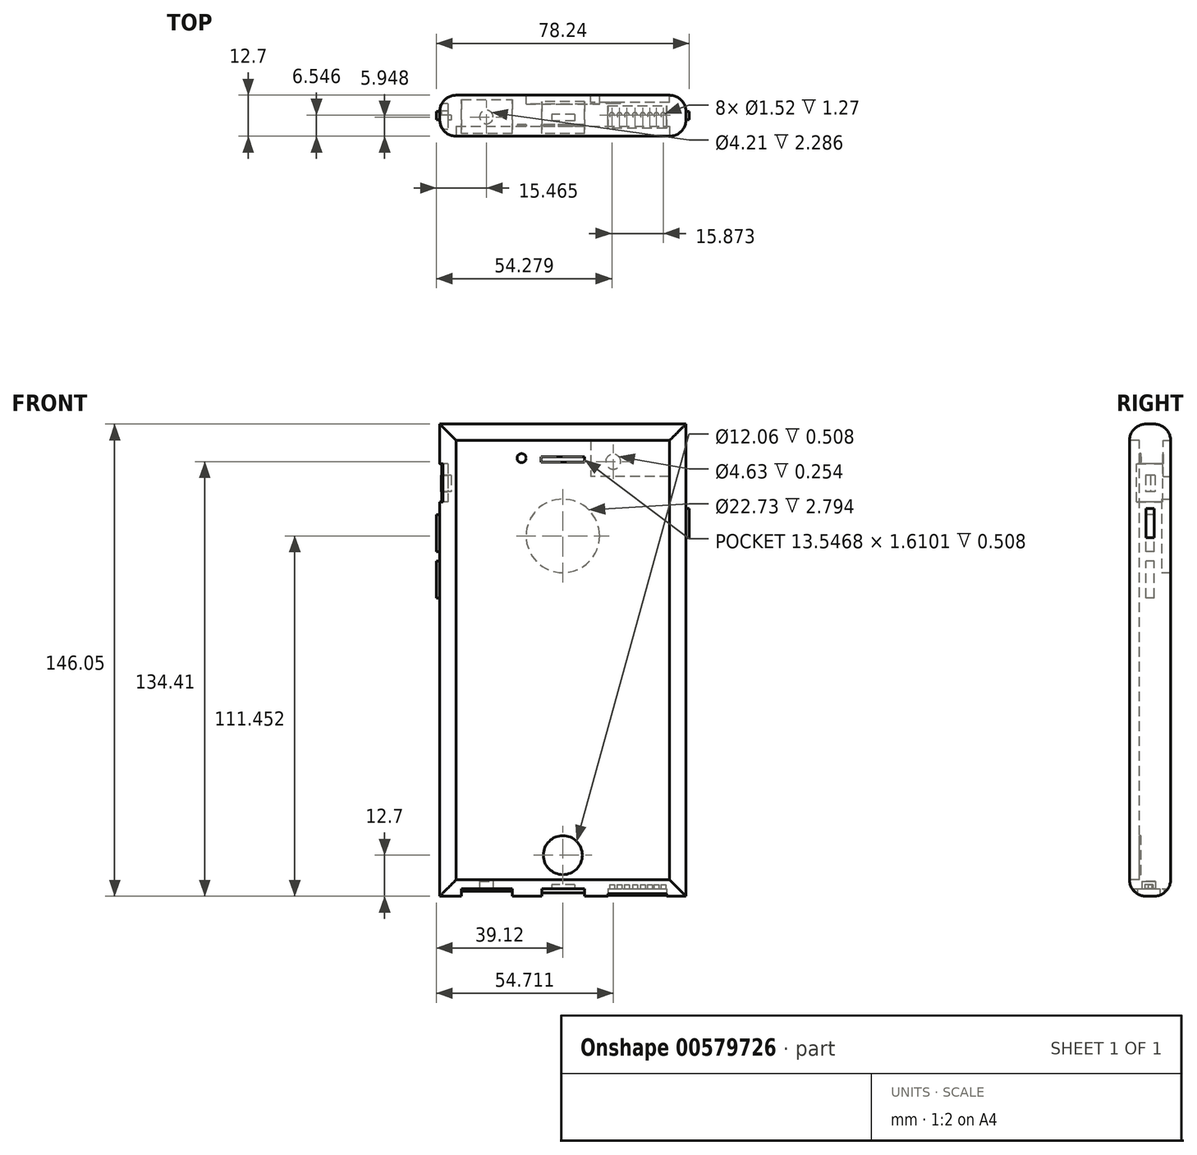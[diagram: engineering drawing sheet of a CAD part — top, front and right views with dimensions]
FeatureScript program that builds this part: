
annotation { "Feature Type Name" : "Feature", "Feature Type Description" : "" }
export const myFeature = defineFeature(function(context is Context, id is Id, definition is map)
    precondition{}
    {
        {
            var Q0;
            Q0=qCreatedBy(makeId("Front.planeOp"),FACE);
            var sketch = newSketch(context, id + "F0", { "sketchPlane" : qUnion([Q0])});
            skLineSegment(sketch, "E0.bottom", {"start": v(0, 0) * mm, "end": v(76.2, 0) * mm});
            skLineSegment(sketch, "E0.top", {"start": v(0, 146.05) * mm, "end": v(76.2, 146.05) * mm});
            skLineSegment(sketch, "E0.left", {"start": v(0, 0) * mm, "end": v(0, 146.05) * mm});
            skLineSegment(sketch, "E0.right", {"start": v(76.2, 0) * mm, "end": v(76.2, 146.05) * mm});
            skSolve(sketch);
        }
        {
            var Q0;
            Q0=makeQuery(id+"F0.imprint","IMPRINT",FACE,{"disambiguationData":[TD([[makeQuery(id+"F0.imprint","IMPRINT",EDGE,{"derivedFrom":sQuery(id+"F0.wireOp",EDGE,"E0.bottom")}),1.0]])]});
            extrude(context, id + "F1", {"entities" : qUnion([Q0]), "depth" : 12.7 * mm, "offsetDistance" : 25.4 * mm});
        }
        {
            var Q0;
            Q0=makeQuery(id+"F1.opExtrude","CAP_FACE",FACE,{"disambiguationData":[OSD([sQuery(id+"F0.wireOp",EDGE,"E0.bottom"),sQuery(id+"F0.wireOp",EDGE,"E0.top"),sQuery(id+"F0.wireOp",EDGE,"E0.left"),sQuery(id+"F0.wireOp",EDGE,"E0.right")])],"isStart":false});
            fillet(context, id + "F2", {"entities" : qUnion([Q0]), "radius" : 5.08 * mm, "tangentPropagation" : true, "allowEdgeOverflow" : false});
        }
        {
            var Q0;
            Q0=makeQuery(id+"F1.opExtrude","CAP_FACE",FACE,{"disambiguationData":[OSD([sQuery(id+"F0.wireOp",EDGE,"E0.bottom"),sQuery(id+"F0.wireOp",EDGE,"E0.top"),sQuery(id+"F0.wireOp",EDGE,"E0.left"),sQuery(id+"F0.wireOp",EDGE,"E0.right")])],"isStart":true});
            fillet(context, id + "F3", {"entities" : qUnion([Q0]), "radius" : 5.08 * mm, "tangentPropagation" : true, "allowEdgeOverflow" : false});
        }
        {
            var Q0;
            Q0=makeQuery(id+"F1.opExtrude","CAP_FACE",FACE,{"disambiguationData":[OSD([sQuery(id+"F0.wireOp",EDGE,"E0.bottom"),sQuery(id+"F0.wireOp",EDGE,"E0.top"),sQuery(id+"F0.wireOp",EDGE,"E0.left"),sQuery(id+"F0.wireOp",EDGE,"E0.right")])],"isStart":false});
            extrude(context, id + "F4", {"entities" : qUnion([Q0]), "operationType" : NewBodyOperationType.REMOVE, "oppositeDirection" : true, "depth" : 2.54 * mm, "offsetDistance" : 25.4 * mm});
        }
        {
            var Q0;
            Q0=makeQuery(id+"F1.opExtrude","SWEPT_FACE",FACE,{"disambiguationData":[OSD([sQuery(id+"F0.wireOp",EDGE,"E0.left")])]});
            var sketch = newSketch(context, id + "F5", { "sketchPlane" : qUnion([Q0])});
            skLineSegment(sketch, "E1.bottom", {"start": v(2.58, 133.75) * mm, "end": v(10.56, 133.75) * mm});
            skLineSegment(sketch, "E1.top", {"start": v(2.58, 122) * mm, "end": v(10.56, 122) * mm});
            skLineSegment(sketch, "E1.left", {"start": v(2.58, 133.75) * mm, "end": v(2.58, 122) * mm});
            skLineSegment(sketch, "E1.right", {"start": v(10.56, 133.75) * mm, "end": v(10.56, 122) * mm});
            skSolve(sketch);
        }
        {
            var Q0;
            {var subQ0=sQuery(id+"F5.wireOp",EDGE,"E1.left");Q0=makeQuery(id+"F5.imprint","IMPRINT",FACE,{"disambiguationData":[TD([[makeQuery(id+"F5.imprint","IMPRINT",EDGE,{"derivedFrom":subQ0}),1.0]])]});}
            var Q1;
            {var subQ0=sQuery(id+"F5.wireOp",EDGE,"E1.bottom");var subQ1=sQuery(id+"F0.wireOp",EDGE,"E0.left");var subQ2=makeQuery(id+"F1.opExtrude","SWEPT_FACE",FACE,{"disambiguationData":[OSD([subQ1])]});var subQ3=makeQuery(id+"F3.opFillet","BLEND_EDGE",EDGE,{"blendedFrom":[makeQuery(id+"F1.opExtrude","CAP_EDGE",EDGE,{"disambiguationData":[OSD([subQ1])],"isStart":true}),subQ2],"blendedInto":[subQ2]});var subQ4=makeQuery(id+"F5.imprint","INTERSECT",VERTEX,{"derivedFrom":[subQ3,subQ0]});Q1=makeQuery(id+"F5.imprint","IMPRINT",FACE,{"disambiguationData":[TD([[makeQuery(id+"F5.imprint","IMPRINT",EDGE,{"disambiguationData":[TD([[subQ4,-1.0]])],"derivedFrom":subQ0}),-1.0]])]});}
            var Q2;
            {var subQ0=sQuery(id+"F5.wireOp",EDGE,"E1.right");Q2=makeQuery(id+"F5.imprint","IMPRINT",FACE,{"disambiguationData":[TD([[makeQuery(id+"F5.imprint","IMPRINT",EDGE,{"derivedFrom":subQ0}),-1.0]])]});}
            extrude(context, id + "F6", {"entities" : qUnion([Q0, Q1, Q2]), "operationType" : NewBodyOperationType.REMOVE, "oppositeDirection" : true, "depth" : 2.54 * mm, "offsetDistance" : 25.4 * mm});
        }
        {
            var Q0;
            Q0=makeQuery(id+"F6.boolean.opBoolean","COPY",FACE,{"derivedFrom":makeQuery(id+"F6.opExtrude","CAP_FACE",FACE,{"disambiguationData":[OSD([sQuery(id+"F5.wireOp",EDGE,"E1.bottom"),sQuery(id+"F5.wireOp",EDGE,"E1.top"),sQuery(id+"F5.wireOp",EDGE,"E1.left"),sQuery(id+"F5.wireOp",EDGE,"E1.right")])],"isStart":false})});
            var sketch = newSketch(context, id + "F7", { "sketchPlane" : qUnion([Q0])});
            skLineSegment(sketch, "E2.bottom", {"start": v(4.8, 130.2) * mm, "end": v(7.68, 130.2) * mm});
            skLineSegment(sketch, "E2.top", {"start": v(4.8, 125.1) * mm, "end": v(7.68, 125.1) * mm});
            skLineSegment(sketch, "E2.left", {"start": v(4.8, 130.2) * mm, "end": v(4.8, 125.1) * mm});
            skLineSegment(sketch, "E2.right", {"start": v(7.68, 130.2) * mm, "end": v(7.68, 125.1) * mm});
            skSolve(sketch);
        }
        {
            var Q0;
            Q0 = qSketchRegion(id + "F7", true);
            extrude(context, id + "F8", {"entities" : qUnion([Q0]), "operationType" : NewBodyOperationType.ADD, "depth" : 2.03 * mm, "offsetDistance" : 25.4 * mm});
        }
        {
            var Q0;
            Q0=makeQuery(id+"F8.opExtrude","CAP_FACE",FACE,{"disambiguationData":[OSD([sQuery(id+"F7.wireOp",EDGE,"E2.bottom"),sQuery(id+"F7.wireOp",EDGE,"E2.top"),sQuery(id+"F7.wireOp",EDGE,"E2.left"),sQuery(id+"F7.wireOp",EDGE,"E2.right")])],"isStart":false});
            var sketch = newSketch(context, id + "F9", { "sketchPlane" : qUnion([Q0])});
            skLineSegment(sketch, "E3", {"start": v(7.68, 125.1) * mm, "end": v(7.68, 130.2) * mm});
            skLineSegment(sketch, "E4", {"start": v(7.68, 130.2) * mm, "end": v(6.24, 130.2) * mm});
            skLineSegment(sketch, "E5", {"start": v(6.24, 130.2) * mm, "end": v(6.24, 125.1) * mm});
            skLineSegment(sketch, "E6", {"start": v(6.24, 125.1) * mm, "end": v(7.68, 125.1) * mm});
            skSolve(sketch);
        }
        {
            var Q0;
            Q0=makeQuery(id+"F9.imprint","IMPRINT",FACE,{"disambiguationData":[TD([[makeQuery(id+"F9.imprint","IMPRINT",EDGE,{"derivedFrom":sQuery(id+"F9.wireOp",EDGE,"E3")}),-1.0]])]});
            extrude(context, id + "F10", {"entities" : qUnion([Q0]), "operationType" : NewBodyOperationType.REMOVE, "oppositeDirection" : true, "depth" : 3.05 * mm, "offsetDistance" : 25.4 * mm});
        }
        {
            var Q0;
            {var subQ0=sQuery(id+"F0.wireOp",EDGE,"E0.bottom");var subQ1=sQuery(id+"F0.wireOp",EDGE,"E0.left");Q0=makeQuery(id+"F6.boolean.opBoolean","SPLIT",FACE,{"disambiguationData":[TD([makeQuery(id+"F1.opExtrude","SWEPT_FACE",FACE,{"disambiguationData":[OSD([subQ0])]})])],"derivedFrom":makeQuery(id+"F1.opExtrude","SWEPT_FACE",FACE,{"disambiguationData":[OSD([subQ1])]})});}
            var sketch = newSketch(context, id + "F11", { "sketchPlane" : qUnion([Q0])});
            skLineSegment(sketch, "E7.bottom", {"start": v(5.08, 118.03) * mm, "end": v(7.62, 118.03) * mm});
            skLineSegment(sketch, "E7.top", {"start": v(5.08, 106.6) * mm, "end": v(7.62, 106.6) * mm});
            skLineSegment(sketch, "E7.left", {"start": v(5.08, 118.03) * mm, "end": v(5.08, 106.6) * mm});
            skLineSegment(sketch, "E7.right", {"start": v(7.62, 118.03) * mm, "end": v(7.62, 106.6) * mm});
            skSolve(sketch);
        }
        {
            var Q0;
            Q0=makeQuery(id+"F11.imprint","IMPRINT",FACE,{"disambiguationData":[TD([[makeQuery(id+"F11.imprint","IMPRINT",EDGE,{"derivedFrom":sQuery(id+"F11.wireOp",EDGE,"E7.bottom")}),-1.0]])]});
            extrude(context, id + "F12", {"entities" : qUnion([Q0]), "operationType" : NewBodyOperationType.ADD, "depth" : 1.02 * mm, "offsetDistance" : 25.4 * mm});
        }
        {
            var Q0;
            {var subQ0=sQuery(id+"F0.wireOp",EDGE,"E0.bottom");var subQ2=sQuery(id+"F0.wireOp",EDGE,"E0.left");var subQ5=makeQuery(id+"F1.opExtrude","SWEPT_FACE",FACE,{"disambiguationData":[OSD([subQ0])]});Q0=makeQuery(id+"F12.boolean.opBoolean","SPLIT",FACE,{"disambiguationData":[TD([subQ5])],"derivedFrom":makeQuery(id+"F6.boolean.opBoolean","SPLIT",FACE,{"disambiguationData":[TD([subQ5])],"derivedFrom":makeQuery(id+"F1.opExtrude","SWEPT_FACE",FACE,{"disambiguationData":[OSD([subQ2])]})})});}
            var sketch = newSketch(context, id + "F13", { "sketchPlane" : qUnion([Q0])});
            skLineSegment(sketch, "E8.bottom", {"start": v(5.08, 103.7) * mm, "end": v(7.62, 103.7) * mm});
            skLineSegment(sketch, "E8.top", {"start": v(5.08, 92.27) * mm, "end": v(7.62, 92.27) * mm});
            skLineSegment(sketch, "E8.left", {"start": v(5.08, 103.7) * mm, "end": v(5.08, 92.27) * mm});
            skLineSegment(sketch, "E8.right", {"start": v(7.62, 103.7) * mm, "end": v(7.62, 92.27) * mm});
            skSolve(sketch);
        }
        {
            var Q0;
            Q0=makeQuery(id+"F13.imprint","IMPRINT",FACE,{"disambiguationData":[TD([[makeQuery(id+"F13.imprint","IMPRINT",EDGE,{"derivedFrom":sQuery(id+"F13.wireOp",EDGE,"E8.bottom")}),-1.0]])]});
            extrude(context, id + "F14", {"entities" : qUnion([Q0]), "operationType" : NewBodyOperationType.ADD, "depth" : 1.02 * mm, "offsetDistance" : 25.4 * mm});
        }
        {
            var Q0;
            Q0=makeQuery(id+"F4.boolean.opBoolean","COPY",FACE,{"derivedFrom":makeQuery(id+"F4.opExtrude","CAP_FACE",FACE,{"disambiguationData":[OSD([sQuery(id+"F0.wireOp",EDGE,"E0.bottom"),sQuery(id+"F0.wireOp",EDGE,"E0.top"),sQuery(id+"F0.wireOp",EDGE,"E0.left"),sQuery(id+"F0.wireOp",EDGE,"E0.right")])],"isStart":false})});
            var sketch = newSketch(context, id + "F15", { "sketchPlane" : qUnion([Q0])});
            skLineSegment(sketch, "E9", {"start": v(5.08, 5.08) * mm, "end": v(38.1, 5.08) * mm});
            skLineSegment(sketch, "E10", {"start": v(38.1, 5.08) * mm, "end": v(38.1, 12.7) * mm});
            skCircle(sketch, "E11", {"center": v(38.1, 12.7) * mm, "radius": 6.03 * mm});
            skSolve(sketch);
        }
        {
            var Q0;
            Q0=makeQuery(id+"F15.imprint","IMPRINT",FACE,{"disambiguationData":[TD([[makeQuery(id+"F15.imprint","IMPRINT",EDGE,{"derivedFrom":sQuery(id+"F15.wireOp",EDGE,"E11")}),1.0]])]});
            extrude(context, id + "F16", {"entities" : qUnion([Q0]), "operationType" : NewBodyOperationType.REMOVE, "oppositeDirection" : true, "depth" : 0.5 * mm, "offsetDistance" : 25.4 * mm});
        }
        {
            var Q0;
            Q0=makeQuery(id+"F1.opExtrude","SWEPT_FACE",FACE,{"disambiguationData":[OSD([sQuery(id+"F0.wireOp",EDGE,"E0.bottom")])]});
            var sketch = newSketch(context, id + "F17", { "sketchPlane" : qUnion([Q0])});
            skLineSegment(sketch, "E12.bottom", {"start": v(6.77, 11.85) * mm, "end": v(22.5, 11.85) * mm});
            skLineSegment(sketch, "E12.top", {"start": v(6.77, 1.38) * mm, "end": v(22.5, 1.38) * mm});
            skLineSegment(sketch, "E12.left", {"start": v(6.77, 11.85) * mm, "end": v(6.77, 1.38) * mm});
            skLineSegment(sketch, "E12.right", {"start": v(22.5, 11.85) * mm, "end": v(22.5, 1.38) * mm});
            skSolve(sketch);
        }
        {
            var Q0;
            Q0 = qSketchRegion(id + "F17", true);
            var Q1;
            {var subQ0=sQuery(id+"F17.wireOp",EDGE,"E12.bottom");Q1=makeQuery(id+"F17.imprint","IMPRINT",FACE,{"disambiguationData":[TD([[makeQuery(id+"F17.imprint","IMPRINT",EDGE,{"derivedFrom":subQ0}),-1.0]])]});}
            extrude(context, id + "F18", {"entities" : qUnion([Q0, Q1]), "operationType" : NewBodyOperationType.REMOVE, "oppositeDirection" : true, "depth" : 2.3 * mm, "offsetDistance" : 25.4 * mm});
        }
        {
            var Q0;
            {var subQ0=sQuery(id+"F0.wireOp",EDGE,"E0.bottom");var subQ2=sQuery(id+"F0.wireOp",EDGE,"E0.right");var subQ5=makeQuery(id+"F1.opExtrude","SWEPT_FACE",FACE,{"disambiguationData":[OSD([subQ2])]});Q0=makeQuery(id+"FUvdi6jXHZb6WJ3_1.boolean.opBoolean","SPLIT",FACE,{"disambiguationData":[TD([subQ5])],"derivedFrom":makeQuery(id+"F18.boolean.opBoolean","SPLIT",FACE,{"disambiguationData":[TD([subQ5])],"derivedFrom":makeQuery(id+"F1.opExtrude","SWEPT_FACE",FACE,{"disambiguationData":[OSD([subQ0])]})})});}
            var sketch = newSketch(context, id + "F19", { "sketchPlane" : qUnion([Q0])});
            skLineSegment(sketch, "E13.bottom", {"start": v(52.05, 10.24) * mm, "end": v(70.18, 10.24) * mm});
            skLineSegment(sketch, "E13.top", {"start": v(52.05, 3.29) * mm, "end": v(70.18, 3.29) * mm});
            skLineSegment(sketch, "E13.left", {"start": v(52.05, 10.24) * mm, "end": v(52.05, 3.29) * mm});
            skLineSegment(sketch, "E13.right", {"start": v(70.18, 10.24) * mm, "end": v(70.18, 3.29) * mm});
            skSolve(sketch);
        }
        {
            var Q0;
            {var subQ0=sQuery(id+"F19.wireOp",EDGE,"E13.top");Q0=makeQuery(id+"F19.imprint","IMPRINT",FACE,{"disambiguationData":[TD([[makeQuery(id+"F19.imprint","IMPRINT",EDGE,{"derivedFrom":subQ0}),1.0]])]});}
            var Q1;
            {var subQ0=sQuery(id+"F19.wireOp",EDGE,"E13.left");var subQ1=sQuery(id+"F0.wireOp",EDGE,"E0.right");var subQ3=sQuery(id+"F0.wireOp",EDGE,"E0.bottom");var subQ5=makeQuery(id+"F1.opExtrude","SWEPT_FACE",FACE,{"disambiguationData":[OSD([subQ1])]});var subQ6=makeQuery(id+"F1.opExtrude","SWEPT_FACE",FACE,{"disambiguationData":[OSD([subQ3])]});var subQ9=makeQuery(id+"FUvdi6jXHZb6WJ3_1.boolean.opBoolean","SPLIT",EDGE,{"disambiguationData":[TD([subQ5])],"derivedFrom":makeQuery(id+"F18.boolean.opBoolean","SPLIT",EDGE,{"disambiguationData":[TD([subQ5])],"derivedFrom":makeQuery(id+"F2.opFillet","BLEND_EDGE",EDGE,{"blendedFrom":[makeQuery(id+"F1.opExtrude","CAP_EDGE",EDGE,{"disambiguationData":[OSD([subQ3])],"isStart":false}),subQ6],"blendedInto":[subQ6]})})});var subQ10=makeQuery(id+"F19.imprint","INTERSECT",VERTEX,{"derivedFrom":[subQ9,subQ0]});Q1=makeQuery(id+"F19.imprint","IMPRINT",FACE,{"disambiguationData":[TD([[makeQuery(id+"F19.imprint","IMPRINT",EDGE,{"disambiguationData":[TD([[subQ10,-1.0]])],"derivedFrom":subQ0}),1.0]])]});}
            var Q2;
            {var subQ0=sQuery(id+"F19.wireOp",EDGE,"E13.bottom");Q2=makeQuery(id+"F19.imprint","IMPRINT",FACE,{"disambiguationData":[TD([[makeQuery(id+"F19.imprint","IMPRINT",EDGE,{"derivedFrom":subQ0}),-1.0]])]});}
            extrude(context, id + "F20", {"entities" : qUnion([Q0, Q1, Q2]), "operationType" : NewBodyOperationType.REMOVE, "oppositeDirection" : true, "depth" : 2.3 * mm, "offsetDistance" : 25.4 * mm});
        }
        {
            var Q0;
            Q0=makeQuery(id+"F18.boolean.opBoolean","COPY",FACE,{"derivedFrom":makeQuery(id+"F18.opExtrude","CAP_FACE",FACE,{"disambiguationData":[OSD([sQuery(id+"F17.wireOp",EDGE,"E12.bottom"),sQuery(id+"F17.wireOp",EDGE,"E12.top"),sQuery(id+"F17.wireOp",EDGE,"E12.left"),sQuery(id+"F17.wireOp",EDGE,"E12.right")])],"isStart":false})});
            var sketch = newSketch(context, id + "F21", { "sketchPlane" : qUnion([Q0])});
            skCircle(sketch, "E14", {"center": v(14.44, 6.75) * mm, "radius": 2.1 * mm});
            skSolve(sketch);
        }
        {
            var Q0;
            Q0 = qSketchRegion(id + "F21", true);
            extrude(context, id + "F22", {"entities" : qUnion([Q0]), "operationType" : NewBodyOperationType.REMOVE, "oppositeDirection" : true, "depth" : 2.3 * mm, "offsetDistance" : 25.4 * mm});
        }
        {
            var Q0;
            Q0=makeQuery(id+"F20.boolean.opBoolean","COPY",FACE,{"derivedFrom":makeQuery(id+"F20.opExtrude","CAP_FACE",FACE,{"disambiguationData":[OSD([sQuery(id+"F19.wireOp",EDGE,"E13.bottom"),sQuery(id+"F19.wireOp",EDGE,"E13.top"),sQuery(id+"F19.wireOp",EDGE,"E13.left"),sQuery(id+"F19.wireOp",EDGE,"E13.right")])],"isStart":false})});
            var sketch = newSketch(context, id + "F23", { "sketchPlane" : qUnion([Q0])});
            skLineSegment(sketch, "E15", {"start": v(52.05, 6.15) * mm, "end": v(70.18, 6.15) * mm});
            skCircle(sketch, "E16", {"center": v(53.26, 6.15) * mm, "radius": 0.76 * mm});
            skCircle(sketch, "E17", {"center": v(55.62, 6.15) * mm, "radius": 0.76 * mm});
            skCircle(sketch, "E18", {"center": v(57.9, 6.15) * mm, "radius": 0.76 * mm});
            skCircle(sketch, "E19", {"center": v(60.4, 6.15) * mm, "radius": 0.76 * mm});
            skCircle(sketch, "E20", {"center": v(62.83, 6.15) * mm, "radius": 0.76 * mm});
            skCircle(sketch, "E21", {"center": v(65.04, 6.15) * mm, "radius": 0.76 * mm});
            skCircle(sketch, "E22", {"center": v(67.06, 6.15) * mm, "radius": 0.76 * mm});
            skCircle(sketch, "E23", {"center": v(69.13, 6.15) * mm, "radius": 0.76 * mm});
            skSolve(sketch);
        }
        {
            var Q0;
            Q0 = qSketchRegion(id + "F23", true);
            extrude(context, id + "F24", {"entities" : qUnion([Q0]), "operationType" : NewBodyOperationType.REMOVE, "oppositeDirection" : true, "depth" : 1.27 * mm, "offsetDistance" : 25.4 * mm});
        }
        {
            var Q0;
            Q0=makeQuery(id+"F16.boolean.opBoolean","COPY",FACE,{"derivedFrom":makeQuery(id+"F16.opExtrude","CAP_FACE",FACE,{"disambiguationData":[OSD([sQuery(id+"F15.wireOp",EDGE,"E11")])],"isStart":false})});
            var sketch = newSketch(context, id + "F25", { "sketchPlane" : qUnion([Q0])});
            skLineSegment(sketch, "E24.bottom", {"start": v(44.87, 135.88) * mm, "end": v(31.33, 135.88) * mm});
            skLineSegment(sketch, "E24.top", {"start": v(44.87, 134.27) * mm, "end": v(31.33, 134.27) * mm});
            skLineSegment(sketch, "E24.left", {"start": v(44.87, 135.88) * mm, "end": v(44.87, 134.27) * mm});
            skLineSegment(sketch, "E24.right", {"start": v(31.33, 135.88) * mm, "end": v(31.33, 134.27) * mm});
            skPoint(sketch, "E24.middle", {"position": v(38.1, 135.08) * mm});
            skSolve(sketch);
        }
        {
            var Q0;
            Q0 = qSketchRegion(id + "F25", true);
            var Q1;
            Q1=makeQuery(id+"F4.boolean.opBoolean","COPY",FACE,{"derivedFrom":makeQuery(id+"F4.opExtrude","CAP_FACE",FACE,{"disambiguationData":[OSD([sQuery(id+"F0.wireOp",EDGE,"E0.bottom"),sQuery(id+"F0.wireOp",EDGE,"E0.top"),sQuery(id+"F0.wireOp",EDGE,"E0.left"),sQuery(id+"F0.wireOp",EDGE,"E0.right")])],"isStart":false})});
            extrude(context, id + "F26", {"entities" : qUnion([Q0, Q1]), "operationType" : NewBodyOperationType.REMOVE, "oppositeDirection" : true, "depth" : 0.5 * mm, "offsetDistance" : 25.4 * mm});
        }
        {
            var Q0;
            Q0=makeQuery(id+"F26.boolean.opBoolean","MERGE",FACE,{"derivedFrom":[makeQuery(id+"F16.boolean.opBoolean","COPY",FACE,{"derivedFrom":makeQuery(id+"F16.opExtrude","CAP_FACE",FACE,{"disambiguationData":[OSD([sQuery(id+"F15.wireOp",EDGE,"E11")])],"isStart":false})}),makeQuery(id+"F26.opExtrude","CAP_FACE",FACE,{"disambiguationData":[OSD([sQuery(id+"F0.wireOp",EDGE,"E0.bottom"),sQuery(id+"F0.wireOp",EDGE,"E0.top"),sQuery(id+"F0.wireOp",EDGE,"E0.left"),sQuery(id+"F0.wireOp",EDGE,"E0.right")])],"isStart":false})]});
            var sketch = newSketch(context, id + "F27", { "sketchPlane" : qUnion([Q0])});
            skCircle(sketch, "E25", {"center": v(25.32, 135.5) * mm, "radius": 1.4 * mm});
            skSolve(sketch);
        }
        {
            var Q0;
            Q0=makeQuery(id+"F27.imprint","IMPRINT",FACE,{"disambiguationData":[TD([[makeQuery(id+"F27.imprint","IMPRINT",EDGE,{"derivedFrom":sQuery(id+"F27.wireOp",EDGE,"E25")}),1.0]])]});
            extrude(context, id + "F28", {"entities" : qUnion([Q0]), "operationType" : NewBodyOperationType.REMOVE, "oppositeDirection" : true, "depth" : 0.5 * mm, "offsetDistance" : 25.4 * mm});
        }
        {
            var Q0;
            Q0=makeQuery(id+"F26.boolean.opBoolean","MERGE",FACE,{"derivedFrom":[makeQuery(id+"F16.boolean.opBoolean","COPY",FACE,{"derivedFrom":makeQuery(id+"F16.opExtrude","CAP_FACE",FACE,{"disambiguationData":[OSD([sQuery(id+"F15.wireOp",EDGE,"E11")])],"isStart":false})}),makeQuery(id+"F26.opExtrude","CAP_FACE",FACE,{"disambiguationData":[OSD([sQuery(id+"F0.wireOp",EDGE,"E0.bottom"),sQuery(id+"F0.wireOp",EDGE,"E0.top"),sQuery(id+"F0.wireOp",EDGE,"E0.left"),sQuery(id+"F0.wireOp",EDGE,"E0.right")])],"isStart":false})]});
            var sketch = newSketch(context, id + "F29", { "sketchPlane" : qUnion([Q0])});
            skLineSegment(sketch, "E26", {"start": v(38.1, 5.08) * mm, "end": v(38.1, 12.7) * mm});
            skCircle(sketch, "E27", {"center": v(38.1, 12.7) * mm, "radius": 6.03 * mm});
            skSolve(sketch);
        }
        {
            var Q0;
            Q0=makeQuery(id+"F29.imprint","IMPRINT",FACE,{"disambiguationData":[TD([[makeQuery(id+"F29.imprint","IMPRINT",EDGE,{"derivedFrom":sQuery(id+"F29.wireOp",EDGE,"E27")}),1.0]])]});
            extrude(context, id + "F30", {"entities" : qUnion([Q0]), "operationType" : NewBodyOperationType.REMOVE, "oppositeDirection" : true, "depth" : 0.5 * mm, "offsetDistance" : 25.4 * mm});
        }
        {
            var Q0;
            {var subQ0=sQuery(id+"F0.wireOp",EDGE,"E0.bottom");var subQ2=makeQuery(id+"F18.opExtrude","SWEPT_FACE",FACE,{"disambiguationData":[OSD([sQuery(id+"F17.wireOp",EDGE,"E12.right")])]});var subQ4=sQuery(id+"F0.wireOp",EDGE,"E0.right");Q0=makeQuery(id+"F20.boolean.opBoolean","SPLIT",FACE,{"disambiguationData":[TD([makeQuery(id+"F18.boolean.opBoolean","COPY",FACE,{"derivedFrom":subQ2})])],"derivedFrom":makeQuery(id+"F18.boolean.opBoolean","SPLIT",FACE,{"disambiguationData":[TD([makeQuery(id+"F1.opExtrude","SWEPT_FACE",FACE,{"disambiguationData":[OSD([subQ4])]})])],"derivedFrom":makeQuery(id+"F1.opExtrude","SWEPT_FACE",FACE,{"disambiguationData":[OSD([subQ0])]})})});}
            var sketch = newSketch(context, id + "F31", { "sketchPlane" : qUnion([Q0])});
            skLineSegment(sketch, "E28", {"start": v(38.23, 17.24) * mm, "end": v(38.23, 13.45) * mm});
            skLineSegment(sketch, "E29.bottom", {"start": v(38.23, 13.45) * mm, "end": v(31.63, 13.45) * mm});
            skLineSegment(sketch, "E29.top", {"start": v(38.23, 2.02) * mm, "end": v(31.63, 2.02) * mm});
            skLineSegment(sketch, "E29.left", {"start": v(38.23, 13.45) * mm, "end": v(38.23, 2.02) * mm});
            skLineSegment(sketch, "E29.right", {"start": v(31.63, 13.45) * mm, "end": v(31.63, 2.02) * mm});
            skLineSegment(sketch, "E30.bottom", {"start": v(38.23, 13.45) * mm, "end": v(44.84, 13.45) * mm});
            skLineSegment(sketch, "E30.top", {"start": v(38.23, 2.02) * mm, "end": v(44.84, 2.02) * mm});
            skLineSegment(sketch, "E30.right", {"start": v(44.84, 13.45) * mm, "end": v(44.84, 2.02) * mm});
            skSolve(sketch);
        }
        {
            var Q0;
            {var subQ0=sQuery(id+"F31.wireOp",EDGE,"E29.top");Q0=makeQuery(id+"F31.imprint","IMPRINT",FACE,{"disambiguationData":[TD([[makeQuery(id+"F31.imprint","IMPRINT",EDGE,{"derivedFrom":subQ0}),-1.0]])]});}
            var Q1;
            {var subQ0=sQuery(id+"F31.wireOp",EDGE,"E30.bottom");Q1=makeQuery(id+"F31.imprint","IMPRINT",FACE,{"disambiguationData":[TD([[makeQuery(id+"F31.imprint","IMPRINT",EDGE,{"derivedFrom":subQ0}),-1.0]])]});}
            var Q2;
            {var subQ0=sQuery(id+"F31.wireOp",EDGE,"E30.top");Q2=makeQuery(id+"F31.imprint","IMPRINT",FACE,{"disambiguationData":[TD([[makeQuery(id+"F31.imprint","IMPRINT",EDGE,{"derivedFrom":subQ0}),1.0]])]});}
            var Q3;
            {var subQ0=sQuery(id+"F31.wireOp",EDGE,"E29.right");var subQ1=sQuery(id+"F0.wireOp",EDGE,"E0.bottom");var subQ2=makeQuery(id+"F1.opExtrude","SWEPT_FACE",FACE,{"disambiguationData":[OSD([subQ1])]});var subQ4=makeQuery(id+"F18.opExtrude","SWEPT_FACE",FACE,{"disambiguationData":[OSD([sQuery(id+"F17.wireOp",EDGE,"E12.right")])]});var subQ5=makeQuery(id+"F18.boolean.opBoolean","COPY",FACE,{"derivedFrom":subQ4});var subQ7=sQuery(id+"F0.wireOp",EDGE,"E0.right");var subQ8=makeQuery(id+"F1.opExtrude","SWEPT_FACE",FACE,{"disambiguationData":[OSD([subQ7])]});var subQ9=makeQuery(id+"F20.boolean.opBoolean","SPLIT",EDGE,{"disambiguationData":[TD([subQ5])],"derivedFrom":makeQuery(id+"F18.boolean.opBoolean","SPLIT",EDGE,{"disambiguationData":[TD([subQ8])],"derivedFrom":makeQuery(id+"F2.opFillet","BLEND_EDGE",EDGE,{"blendedFrom":[makeQuery(id+"F1.opExtrude","CAP_EDGE",EDGE,{"disambiguationData":[OSD([subQ1])],"isStart":false}),subQ2],"blendedInto":[subQ2]})})});var subQ10=makeQuery(id+"F31.imprint","INTERSECT",VERTEX,{"derivedFrom":[subQ9,subQ0]});Q3=makeQuery(id+"F31.imprint","IMPRINT",FACE,{"disambiguationData":[TD([[makeQuery(id+"F31.imprint","IMPRINT",EDGE,{"disambiguationData":[TD([[subQ10,-1.0]])],"derivedFrom":subQ0}),1.0]])]});}
            var Q4;
            {var subQ0=sQuery(id+"F31.wireOp",EDGE,"E29.left");var subQ1=sQuery(id+"F0.wireOp",EDGE,"E0.bottom");var subQ2=makeQuery(id+"F1.opExtrude","SWEPT_FACE",FACE,{"disambiguationData":[OSD([subQ1])]});var subQ4=makeQuery(id+"F18.opExtrude","SWEPT_FACE",FACE,{"disambiguationData":[OSD([sQuery(id+"F17.wireOp",EDGE,"E12.right")])]});var subQ5=makeQuery(id+"F18.boolean.opBoolean","COPY",FACE,{"derivedFrom":subQ4});var subQ7=sQuery(id+"F0.wireOp",EDGE,"E0.right");var subQ8=makeQuery(id+"F1.opExtrude","SWEPT_FACE",FACE,{"disambiguationData":[OSD([subQ7])]});var subQ9=makeQuery(id+"F20.boolean.opBoolean","SPLIT",EDGE,{"disambiguationData":[TD([subQ5])],"derivedFrom":makeQuery(id+"F18.boolean.opBoolean","SPLIT",EDGE,{"disambiguationData":[TD([subQ8])],"derivedFrom":makeQuery(id+"F2.opFillet","BLEND_EDGE",EDGE,{"blendedFrom":[makeQuery(id+"F1.opExtrude","CAP_EDGE",EDGE,{"disambiguationData":[OSD([subQ1])],"isStart":false}),subQ2],"blendedInto":[subQ2]})})});var subQ10=makeQuery(id+"F31.imprint","INTERSECT",VERTEX,{"derivedFrom":[subQ9,subQ0]});Q4=makeQuery(id+"F31.imprint","IMPRINT",FACE,{"disambiguationData":[TD([[makeQuery(id+"F31.imprint","IMPRINT",EDGE,{"disambiguationData":[TD([[subQ10,-1.0]])],"derivedFrom":subQ0}),1.0]])]});}
            var Q5;
            {var subQ0=sQuery(id+"F31.wireOp",EDGE,"E29.bottom");Q5=makeQuery(id+"F31.imprint","IMPRINT",FACE,{"disambiguationData":[TD([[makeQuery(id+"F31.imprint","IMPRINT",EDGE,{"derivedFrom":subQ0}),1.0]])]});}
            extrude(context, id + "F32", {"entities" : qUnion([Q0, Q1, Q2, Q3, Q4, Q5]), "operationType" : NewBodyOperationType.REMOVE, "oppositeDirection" : true, "depth" : 2.3 * mm, "offsetDistance" : 25.4 * mm});
        }
        {
            var Q0;
            Q0=makeQuery(id+"F32.boolean.opBoolean","COPY",FACE,{"derivedFrom":makeQuery(id+"F32.opExtrude","CAP_FACE",FACE,{"disambiguationData":[OSD([sQuery(id+"F31.wireOp",EDGE,"E29.bottom"),sQuery(id+"F31.wireOp",EDGE,"E29.top"),sQuery(id+"F31.wireOp",EDGE,"E29.right"),sQuery(id+"F31.wireOp",EDGE,"E30.bottom"),sQuery(id+"F31.wireOp",EDGE,"E30.top"),sQuery(id+"F31.wireOp",EDGE,"E30.right")])],"isStart":false})});
            var sketch = newSketch(context, id + "F33", { "sketchPlane" : qUnion([Q0])});
            skLineSegment(sketch, "E31", {"start": v(31.63, 6.94) * mm, "end": v(38.23, 6.94) * mm});
            skPoint(sketch, "E31.endSnap0", {"position": v(44.84, 6.94) * mm});
            skLineSegment(sketch, "E32.bottom", {"start": v(41.81, 5.89) * mm, "end": v(34.65, 5.89) * mm});
            skLineSegment(sketch, "E32.top", {"start": v(41.81, 8) * mm, "end": v(34.65, 8) * mm});
            skLineSegment(sketch, "E32.left", {"start": v(41.81, 5.89) * mm, "end": v(41.81, 8) * mm});
            skLineSegment(sketch, "E32.right", {"start": v(34.65, 5.89) * mm, "end": v(34.65, 8) * mm});
            skPoint(sketch, "E32.middle", {"position": v(38.23, 6.94) * mm});
            skSolve(sketch);
        }
        {
            var Q0;
            {var subQ1=sQuery(id+"F33.wireOp",EDGE,"E32.bottom");Q0=makeQuery(id+"F33.imprint","IMPRINT",FACE,{"disambiguationData":[TD([[makeQuery(id+"F33.imprint","IMPRINT",EDGE,{"derivedFrom":subQ1}),-1.0]])]});}
            extrude(context, id + "F34", {"entities" : qUnion([Q0]), "operationType" : NewBodyOperationType.REMOVE, "oppositeDirection" : true, "depth" : 1.27 * mm, "offsetDistance" : 25.4 * mm});
        }
        {
            var Q0;
            Q0=makeQuery(id+"F1.opExtrude","CAP_FACE",FACE,{"disambiguationData":[OSD([sQuery(id+"F0.wireOp",EDGE,"E0.bottom"),sQuery(id+"F0.wireOp",EDGE,"E0.top"),sQuery(id+"F0.wireOp",EDGE,"E0.left"),sQuery(id+"F0.wireOp",EDGE,"E0.right")])],"isStart":true});
            var sketch = newSketch(context, id + "F35", { "sketchPlane" : qUnion([Q0])});
            skLineSegment(sketch, "E33.bottom", {"start": v(-71.12, 140.97) * mm, "end": v(-46.68, 140.97) * mm});
            skLineSegment(sketch, "E33.top", {"start": v(-71.12, 129.76) * mm, "end": v(-46.68, 129.76) * mm});
            skLineSegment(sketch, "E33.left", {"start": v(-71.12, 140.97) * mm, "end": v(-71.12, 129.76) * mm});
            skLineSegment(sketch, "E33.right", {"start": v(-46.68, 140.97) * mm, "end": v(-46.68, 129.76) * mm});
            skSolve(sketch);
        }
        {
            var Q0;
            Q0=makeQuery(id+"F35.imprint","IMPRINT",FACE,{"disambiguationData":[TD([[makeQuery(id+"F35.imprint","IMPRINT",EDGE,{"derivedFrom":sQuery(id+"F35.wireOp",EDGE,"E33.bottom")}),1.0]])]});
            extrude(context, id + "F36", {"entities" : qUnion([Q0]), "operationType" : NewBodyOperationType.REMOVE, "oppositeDirection" : true, "depth" : 2.3 * mm, "offsetDistance" : 25.4 * mm});
        }
        {
            var Q0;
            Q0=makeQuery(id+"F36.boolean.opBoolean","COPY",FACE,{"derivedFrom":makeQuery(id+"F36.opExtrude","CAP_FACE",FACE,{"disambiguationData":[OSD([sQuery(id+"F35.wireOp",EDGE,"E33.bottom"),sQuery(id+"F35.wireOp",EDGE,"E33.top"),sQuery(id+"F35.wireOp",EDGE,"E33.left"),sQuery(id+"F35.wireOp",EDGE,"E33.right")])],"isStart":false})});
            var sketch = newSketch(context, id + "F37", { "sketchPlane" : qUnion([Q0])});
            skCircle(sketch, "E34", {"center": v(-64.77, 134.85) * mm, "radius": 3.81 * mm});
            skCircle(sketch, "E35", {"center": v(-53.7, 134.85) * mm, "radius": 2.82 * mm});
            skSolve(sketch);
        }
        {
            var Q0;
            Q0=sQuery(id+"F37.wireOp",EDGE,"E34");
            extrude(context, id + "F38", {"bodyType" : ToolBodyType.SURFACE, "surfaceEntities" : qUnion([Q0]), "depth" : 1.02 * mm, "offsetDistance" : 25.4 * mm});
        }
        {
            var Q0;
            Q0=makeQuery(id+"F36.boolean.opBoolean","COPY",FACE,{"derivedFrom":makeQuery(id+"F36.opExtrude","CAP_FACE",FACE,{"disambiguationData":[OSD([sQuery(id+"F35.wireOp",EDGE,"E33.bottom"),sQuery(id+"F35.wireOp",EDGE,"E33.top"),sQuery(id+"F35.wireOp",EDGE,"E33.left"),sQuery(id+"F35.wireOp",EDGE,"E33.right")])],"isStart":false})});
            var sketch = newSketch(context, id + "F39", { "sketchPlane" : qUnion([Q0])});
            skCircle(sketch, "E36", {"center": v(-53.7, 134.41) * mm, "radius": 2.31 * mm});
            skSolve(sketch);
        }
        {
            var Q0;
            Q0=makeQuery(id+"F39.imprint","IMPRINT",FACE,{"disambiguationData":[TD([[makeQuery(id+"F39.imprint","IMPRINT",EDGE,{"derivedFrom":sQuery(id+"F39.wireOp",EDGE,"E36")}),1.0]])]});
            extrude(context, id + "F40", {"entities" : qUnion([Q0]), "operationType" : NewBodyOperationType.REMOVE, "oppositeDirection" : true, "depth" : 0.25 * mm, "offsetDistance" : 25.4 * mm});
        }
        {
            var Q0;
            Q0=makeQuery(id+"F1.opExtrude","CAP_FACE",FACE,{"disambiguationData":[OSD([sQuery(id+"F0.wireOp",EDGE,"E0.bottom"),sQuery(id+"F0.wireOp",EDGE,"E0.top"),sQuery(id+"F0.wireOp",EDGE,"E0.left"),sQuery(id+"F0.wireOp",EDGE,"E0.right")])],"isStart":true});
            var sketch = newSketch(context, id + "F41", { "sketchPlane" : qUnion([Q0])});
            skLineSegment(sketch, "E37", {"start": v(-5.08, 140.97) * mm, "end": v(-38.1, 140.97) * mm});
            skLineSegment(sketch, "E38", {"start": v(-38.1, 140.97) * mm, "end": v(-38.1, 111.45) * mm});
            skCircle(sketch, "E39", {"center": v(-38.1, 111.45) * mm, "radius": 11.36 * mm});
            skSolve(sketch);
        }
        {
            var Q0;
            Q0 = qSketchRegion(id + "F41", true);
            var Q1;
            Q1=makeQuery(id+"F41.imprint","IMPRINT",FACE,{"disambiguationData":[TD([[makeQuery(id+"F41.imprint","IMPRINT",EDGE,{"derivedFrom":sQuery(id+"F41.wireOp",EDGE,"E39")}),1.0]])]});
            extrude(context, id + "F42", {"entities" : qUnion([Q0, Q1]), "operationType" : NewBodyOperationType.REMOVE, "oppositeDirection" : true, "depth" : 1.02 * mm, "offsetDistance" : 25.4 * mm});
        }
        {
            var Q0;
            Q0=makeQuery(id+"F42.boolean.opBoolean","COPY",FACE,{"derivedFrom":makeQuery(id+"F42.opExtrude","CAP_FACE",FACE,{"disambiguationData":[OSD([sQuery(id+"F41.wireOp",EDGE,"E39")])],"isStart":false})});
            extrude(context, id + "F43", {"entities" : qUnion([Q0]), "operationType" : NewBodyOperationType.REMOVE, "oppositeDirection" : true, "depth" : 1.78 * mm, "offsetDistance" : 25.4 * mm});
        }
        {
            var Q0;
            Q0=makeQuery(id+"F1.opExtrude","SWEPT_FACE",FACE,{"disambiguationData":[OSD([sQuery(id+"F0.wireOp",EDGE,"E0.right")])]});
            var sketch = newSketch(context, id + "F44", { "sketchPlane" : qUnion([Q0])});
            skLineSegment(sketch, "E40.bottom", {"start": v(-5.08, 119.84) * mm, "end": v(-7.62, 119.84) * mm});
            skLineSegment(sketch, "E40.top", {"start": v(-5.08, 110.9) * mm, "end": v(-7.62, 110.9) * mm});
            skLineSegment(sketch, "E40.left", {"start": v(-5.08, 119.84) * mm, "end": v(-5.08, 110.9) * mm});
            skLineSegment(sketch, "E40.right", {"start": v(-7.62, 119.84) * mm, "end": v(-7.62, 110.9) * mm});
            skSolve(sketch);
        }
        {
            var Q0;
            Q0=makeQuery(id+"F44.imprint","IMPRINT",FACE,{"disambiguationData":[TD([[makeQuery(id+"F44.imprint","IMPRINT",EDGE,{"derivedFrom":sQuery(id+"F44.wireOp",EDGE,"E40.bottom")}),1.0]])]});
            extrude(context, id + "F45", {"entities" : qUnion([Q0]), "operationType" : NewBodyOperationType.ADD, "depth" : 1.02 * mm, "offsetDistance" : 25.4 * mm});
        }
    });
